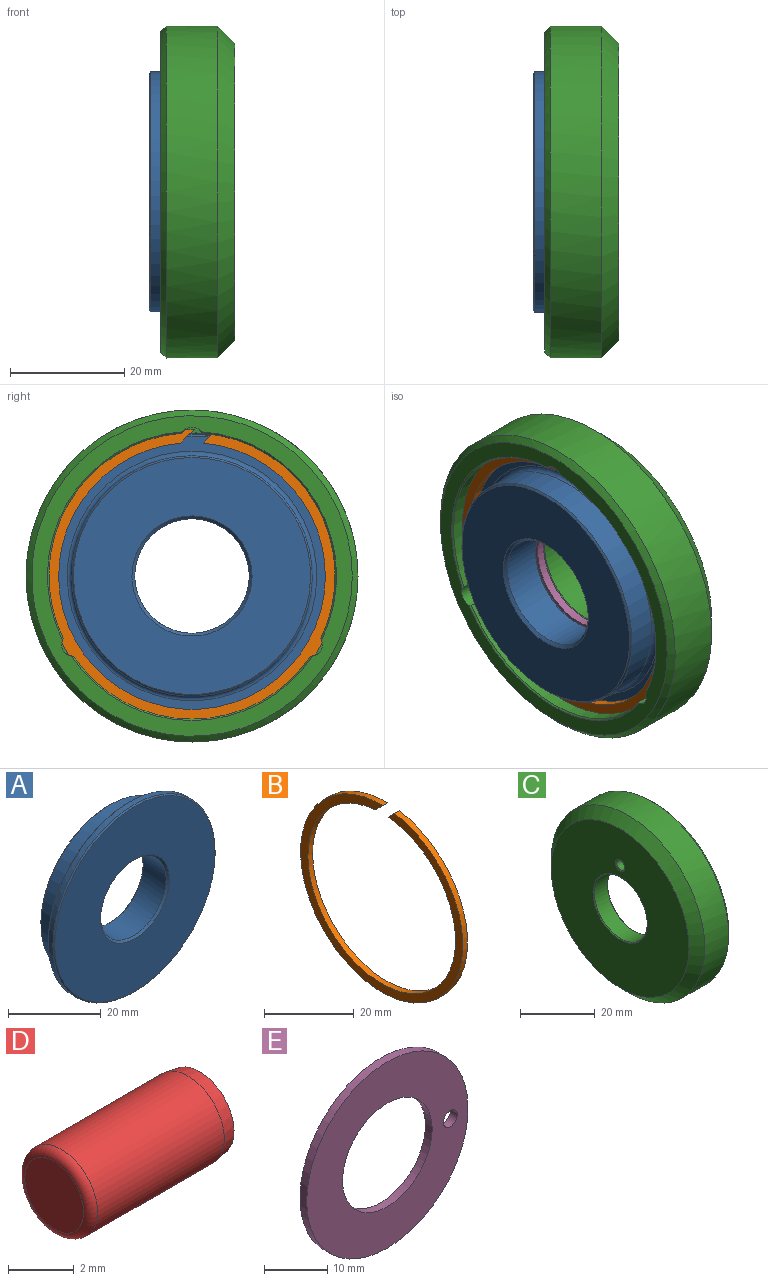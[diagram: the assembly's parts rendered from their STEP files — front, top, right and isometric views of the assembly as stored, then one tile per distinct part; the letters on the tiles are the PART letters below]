
ASSEMBLY  parts=5 mates=9
PART A: 12 faces, bbox 49.5x8x49.5 mm
  f0: plane 48.9x48.9mm, normal (0,1,0), area 385mm2, adj f8,f9
  f1: cylinder r=24.75mm len=49.5mm, axis (0,-1,0), area 217.7mm2, adj f7,f8
  f2: plane 48.9x48.9mm, normal (0,-1,0), area 1531.7mm2, adj f7,f10
  f3: plane 41.4x41.4mm, normal (0,1,0), area 999.8mm2, adj f6,f11
  f4: cylinder r=21mm len=42mm, axis (0,-1,0), area 646.5mm2, adj f6,f9
  f5: cylinder r=10mm len=20mm, axis (0,1,0), area 439.8mm2, adj f10,f11
  f6: cone r=21mm half-angle=45deg, axis (0,-1,0), area 55.6mm2, adj f3,f4
  f7: cone r=24.45mm half-angle=45deg, axis (0,1,0), area 65.6mm2, adj f1,f2
  f8: cone r=24.75mm half-angle=45deg, axis (0,-1,0), area 65.6mm2, adj f0,f1
  f9: torus R=21.8mm, axis (0,-1,0), area 168.1mm2, adj f0,f4
  f10: cone r=10.5mm half-angle=45deg, axis (0,-1,0), area 45.5mm2, adj f2,f5
  f11: cone r=10mm half-angle=45deg, axis (0,1,0), area 45.5mm2, adj f3,f5
PART B: 6 faces, bbox 1.5x51.2x51.2 mm
  f0: plane 51.2x51.2mm, normal (-1,0,0), area 344.5mm2, adj f2,f3,f4,f5
  f1: plane 51.2x51.2mm, normal (1,0,0), area 344.5mm2, adj f2,f3,f4,f5
  f2: cylinder r=25.6mm len=51.2mm, axis (1,0,0), area 235.7mm2, adj f0,f1,f4,f5
  f3: cylinder r=23.3mm len=46.6mm, axis (1,0,0), area 213.6mm2, adj f0,f1,f4,f5
  f4: plane 2.06x2.06mm, normal (0,0.71,0.71), area 4.4mm2, adj f0,f1,f2,f3
  f5: plane 2.38x2.38mm, normal (0,-0.71,-0.71), area 5.1mm2, adj f0,f1,f2,f3
PART C: 33 faces, bbox 13x58x58 mm
  f0: cylinder r=25.6mm len=37.28mm, axis (1,0,0), area 81.8mm2, adj f11,f13,f20,f21
  f1: cylinder r=25.6mm len=43.05mm, axis (1,0,0), area 81.8mm2, adj f3,f11,f19,f20
  f2: plane 37.28x24.36mm, normal (-1,0,0), area 29.9mm2, adj f12,f14,f19,f21
  f3: plane 43.05x11.74mm, normal (-1,0,0), area 29.9mm2, adj f1,f5,f19,f20
  f4: cylinder r=25mm len=35.88mm, axis (1,0,0), area 105mm2, adj f13,f20,f21,f30
  f5: cylinder r=25mm len=41.43mm, axis (1,0,0), area 105mm2, adj f3,f19,f20,f31
  f6: plane 56x56mm, normal (1,0,0), area 455mm2, adj f19,f20,f21,f23,f29,f30,f31
  f7: plane 36.5x36.5mm, normal (1,0,0), area 706mm2, adj f8,f26,f28
  f8: cylinder r=18.25mm len=36.5mm, axis (1,0,0), area 86mm2, adj f7,f24
  f9: plane 49.2x49.2mm, normal (1,0,0), area 826mm2, adj f24,f32
  f10: cylinder r=25mm len=50mm, axis (1,0,0), area 329.9mm2, adj f11,f32
  f11: plane 51.6x51.2mm, normal (1,0,0), area 97.4mm2, adj f0,f1,f10,f12,f19,f20,f21
  f12: cylinder r=25.6mm len=37.28mm, axis (1,0,0), area 81.8mm2, adj f2,f11,f19,f21
  f13: plane 37.28x24.36mm, normal (-1,0,0), area 29.9mm2, adj f0,f4,f20,f21
  f14: cylinder r=25mm len=35.88mm, axis (1,0,0), area 105mm2, adj f2,f19,f21,f29
  f15: cylinder r=29mm len=58mm, axis (1,0,0), area 1639.9mm2, adj f22,f23
  f16: plane 52x52mm, normal (-1,0,0), area 1783.3mm2, adj f22,f25,f27
  f17: cylinder r=10mm len=20mm, axis (1,0,0), area 314.2mm2, adj f25,f26
  f18: cylinder r=1.56mm len=5mm, axis (1,0,0), area 49.1mm2, adj f27,f28
  f19: cylinder r=2mm len=4mm, axis (1,0,0), area 14.6mm2, adj f1,f2,f3,f5,f6,f11,f12,f14
  f20: cylinder r=2mm len=4mm, axis (1,0,0), area 14.6mm2, adj f0,f1,f3,f4,f5,f6,f11,f13
  f21: cylinder r=2mm len=4mm, axis (1,0,0), area 14.6mm2, adj f0,f2,f4,f6,f11,f12,f13,f14
  f22: cone r=29mm half-angle=45deg, axis (1,0,0), area 733.1mm2, adj f15,f16
  f23: cone r=28mm half-angle=45deg, axis (-1,0,0), area 253.2mm2, adj f6,f15
  f24: cone r=18.25mm half-angle=45deg, axis (1,0,0), area 40.8mm2, adj f8,f9
  f25: cone r=10.25mm half-angle=45deg, axis (-1,0,0), area 22.5mm2, adj f16,f17
  f26: cone r=10mm half-angle=45deg, axis (1,0,0), area 22.5mm2, adj f7,f17
  f27: cone r=1.56mm half-angle=45deg, axis (-1,0,0), area 3.7mm2, adj f16,f18
  f28: cone r=1.56mm half-angle=45deg, axis (1,0,0), area 3.7mm2, adj f7,f18
  f29: cone r=25mm half-angle=45deg, axis (1,0,0), area 17.4mm2, adj f6,f14,f19,f21
  f30: cone r=25mm half-angle=45deg, axis (1,0,0), area 17.4mm2, adj f4,f6,f20,f21
  f31: cone r=25mm half-angle=45deg, axis (1,0,0), area 17.4mm2, adj f5,f6,f19,f20
  f32: torus R=24.6mm, axis (1,0,0), area 98.1mm2, adj f9,f10
PART D: 5 faces, bbox 6.3x3.4x3.4 mm
  f0: plane 2.53x2.53mm, normal (-1,0,0), area 5mm2, adj f4
  f1: plane 2.96x2.96mm, normal (1,0,0), area 6.9mm2, adj f2
  f2: cone r=1.56mm half-angle=9.5deg, axis (-1,0,0), area 4.8mm2, adj f1,f3
  f3: cylinder r=1.56mm len=5.45mm, axis (1,0,0), area 53.5mm2, adj f2,f4
  f4: torus R=1.26mm, axis (1,0,0), area 4.3mm2, adj f0,f3
PART E: 5 faces, bbox 36x1.5x36 mm
  f0: plane 36x36mm, normal (0,-1,0), area 696mm2, adj f2,f3,f4
  f1: plane 36x36mm, normal (0,1,0), area 696mm2, adj f2,f3,f4
  f2: cylinder r=18mm len=36mm, axis (0,-1,0), area 169.6mm2, adj f0,f1
  f3: cylinder r=10mm len=20mm, axis (0,-1,0), area 94.2mm2, adj f0,f1
  f4: cylinder r=1.56mm len=3.13mm, axis (0,-1,0), area 14.7mm2, adj f0,f1
PLACE A rot(axis=(0.71,-0.71,0),180deg) t=(83.05,-137.86,-69.45)mm
PLACE B t=(79.45,-137.86,-69.45)mm
PLACE C rot(axis=(0,-0.71,0.71),180deg) t=(90.05,-137.86,-69.45)mm
PLACE D rot(axis=(0,0.61,0.79),0deg) t=(83.8,-151.92,-69.45)mm
PLACE E rot(axis=(0,0,-1),90deg) t=(83.05,-137.86,-69.45)mm
MATE cylindrical D.f2 <-> C.f18  axis (1,0,0) through (89.55,-151.92,-69.45)mm
MATE planar C.f7 <-> E.f1  axis (-1,0,0) through (84.55,-137.66,-69.45)mm
MATE cylindrical A.f5 <-> E.f3  axis (-1,0,0) through (82.55,-137.86,-69.45)mm
MATE cylindrical C.f0 <-> B.f3  axis (-1,0,0) through (78.37,-137.86,-69.45)mm
MATE cylindrical E.f4 <-> C.f18  axis (-1,0,0) through (83.05,-151.92,-69.45)mm
MATE planar C.f16 <-> D.f2  axis (1,0,0) through (90.05,-137.78,-69.45)mm
MATE cylindrical C.f18 <-> E.f4  axis (-1,0,0) through (87.3,-151.92,-69.45)mm
MATE planar C.f0 <-> B.f0  axis (1,0,0) through (79.45,-137.86,-69.45)mm
MATE planar E.f0 <-> A.f1  axis (-1,0,0) through (83.05,-137.71,-69.45)mm
